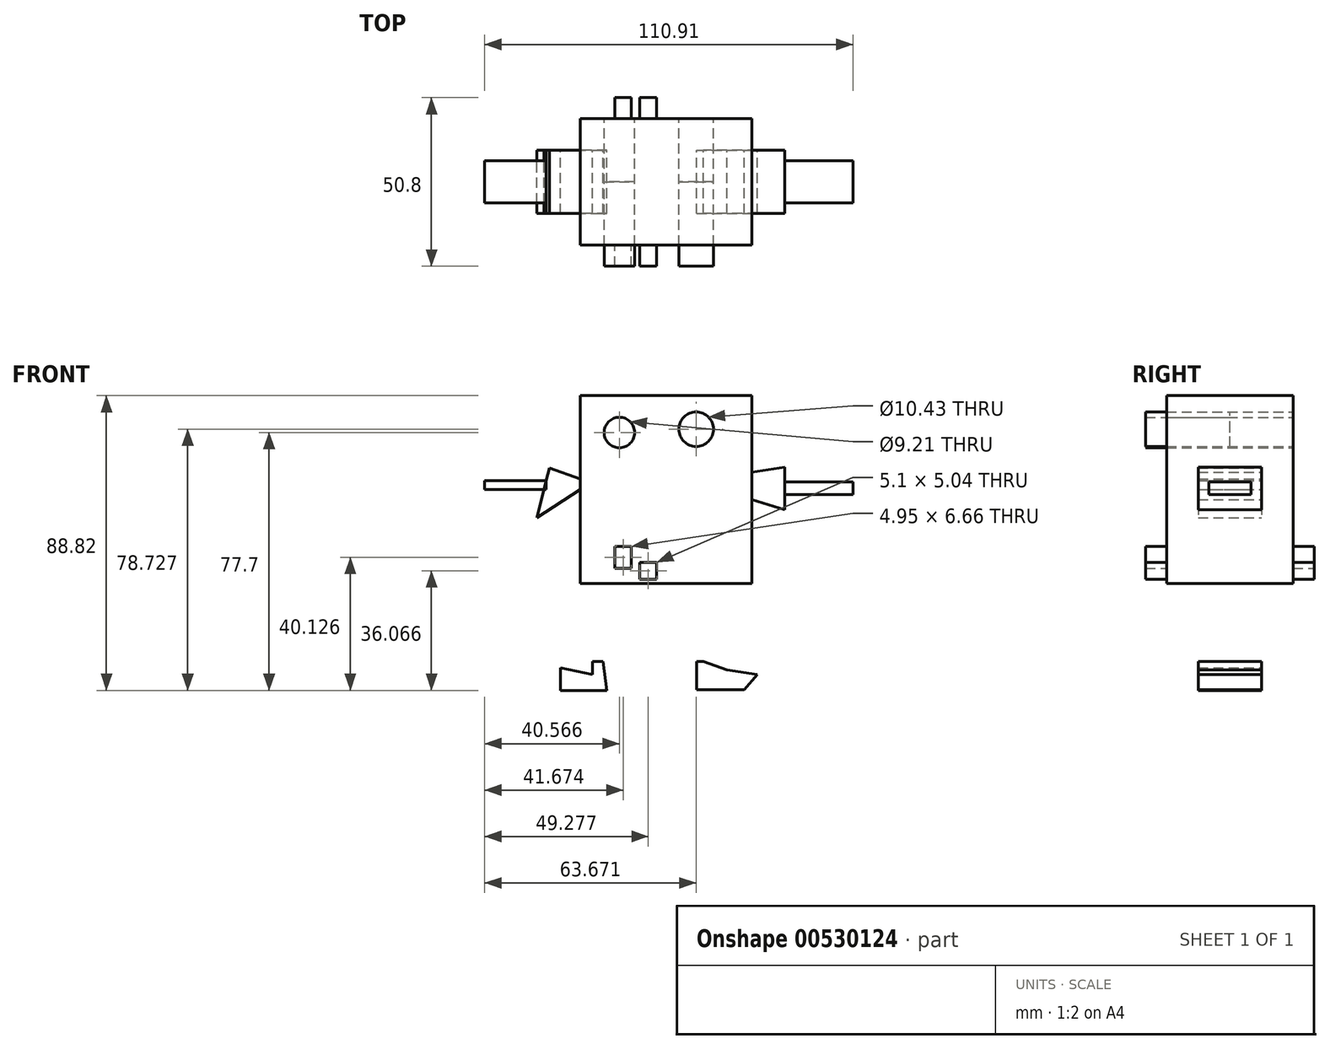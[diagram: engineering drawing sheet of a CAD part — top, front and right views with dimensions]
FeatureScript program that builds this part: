
annotation { "Feature Type Name" : "Feature", "Feature Type Description" : "" }
export const myFeature = defineFeature(function(context is Context, id is Id, definition is map)
    precondition{}
    {
        {
            var Q0;
            Q0=qCreatedBy(makeId("Front.planeOp"),FACE);
            var sketch = newSketch(context, id + "F0", { "sketchPlane" : qUnion([Q0])});
            skLineSegment(sketch, "E0.bottom", {"start": v(-25.84, -28.32) * mm, "end": v(25.84, -28.32) * mm});
            skLineSegment(sketch, "E0.top", {"start": v(-25.84, 28.32) * mm, "end": v(25.84, 28.32) * mm});
            skLineSegment(sketch, "E0.left", {"start": v(-25.84, -28.32) * mm, "end": v(-25.84, 28.32) * mm});
            skLineSegment(sketch, "E0.right", {"start": v(25.84, -28.32) * mm, "end": v(25.84, 28.32) * mm});
            skPoint(sketch, "E0.middle", {"position": v(0, 0) * mm});
            skCircle(sketch, "E1", {"center": v(-14.03, 17.2) * mm, "radius": 4.6 * mm});
            skCircle(sketch, "E2", {"center": v(9.07, 18.23) * mm, "radius": 5.22 * mm});
            skFitSpline(sketch, "E3", {"points": [v(-5.82, 8.64) * mm, v(-4.62, -11.72) * mm, v(3.08, 6.42) * mm], "startDerivative": vector(-0.94, -59.8) * mm, "endDerivative": vector(18.8, 55.68) * mm});
            skArc(sketch, "E4", {"start": v(-14.55, -10.7) * mm, "mid": v(0.62, -22.74) * mm, "end": v(18.65, -15.66) * mm});
            skLineSegment(sketch, "E5.bottom", {"start": v(-10.45, -17.04) * mm, "end": v(-15.4, -17.04) * mm});
            skLineSegment(sketch, "E5.top", {"start": v(-10.45, -23.7) * mm, "end": v(-15.4, -23.7) * mm});
            skLineSegment(sketch, "E5.left", {"start": v(-10.45, -17.04) * mm, "end": v(-10.45, -23.7) * mm});
            skLineSegment(sketch, "E5.right", {"start": v(-15.4, -17.04) * mm, "end": v(-15.4, -23.7) * mm});
            skLineSegment(sketch, "E6.bottom", {"start": v(-2.77, -21.91) * mm, "end": v(-7.87, -21.91) * mm});
            skLineSegment(sketch, "E6.top", {"start": v(-2.77, -26.96) * mm, "end": v(-7.87, -26.96) * mm});
            skLineSegment(sketch, "E6.left", {"start": v(-2.77, -21.91) * mm, "end": v(-2.77, -26.96) * mm});
            skLineSegment(sketch, "E6.right", {"start": v(-7.87, -21.91) * mm, "end": v(-7.87, -26.96) * mm});
            skLineSegment(sketch, "E7.bottom", {"start": v(-22.08, -28.32) * mm, "end": v(-19, -28.32) * mm});
            skLineSegment(sketch, "E7.top", {"start": v(-22.08, -51.77) * mm, "end": v(-19, -51.77) * mm});
            skLineSegment(sketch, "E7.left", {"start": v(-22.08, -28.32) * mm, "end": v(-22.08, -51.77) * mm});
            skLineSegment(sketch, "E7.right", {"start": v(-19, -28.32) * mm, "end": v(-19, -51.77) * mm});
            skLineSegment(sketch, "E8.bottom", {"start": v(9.24, -28.32) * mm, "end": v(11.3, -28.32) * mm});
            skLineSegment(sketch, "E8.top", {"start": v(9.24, -51.77) * mm, "end": v(11.3, -51.77) * mm});
            skLineSegment(sketch, "E8.left", {"start": v(9.24, -28.32) * mm, "end": v(9.24, -51.77) * mm});
            skLineSegment(sketch, "E8.right", {"start": v(11.3, -28.32) * mm, "end": v(11.3, -51.77) * mm});
            skLineSegment(sketch, "E9", {"start": v(-19, -51.77) * mm, "end": v(-17.8, -60.5) * mm});
            skLineSegment(sketch, "E10", {"start": v(-17.8, -60.5) * mm, "end": v(-31.83, -60.5) * mm});
            skLineSegment(sketch, "E11", {"start": v(-31.83, -60.5) * mm, "end": v(-31.83, -53.65) * mm});
            skLineSegment(sketch, "E12", {"start": v(-31.83, -53.65) * mm, "end": v(-22.08, -55.7) * mm});
            skLineSegment(sketch, "E13", {"start": v(-22.08, -55.7) * mm, "end": v(-22.08, -51.77) * mm});
            skLineSegment(sketch, "E14", {"start": v(9.24, -51.77) * mm, "end": v(9.24, -60.33) * mm});
            skLineSegment(sketch, "E15", {"start": v(9.24, -60.33) * mm, "end": v(23.62, -60.33) * mm});
            skLineSegment(sketch, "E16", {"start": v(23.62, -60.33) * mm, "end": v(27.55, -55.7) * mm});
            skLineSegment(sketch, "E17", {"start": v(27.55, -55.7) * mm, "end": v(18.31, -54.34) * mm});
            skLineSegment(sketch, "E18", {"start": v(18.31, -54.34) * mm, "end": v(11.3, -51.77) * mm});
            skLineSegment(sketch, "E19", {"start": v(-25.84, 3.17) * mm, "end": v(-35.12, 6.56) * mm});
            skLineSegment(sketch, "E20", {"start": v(-35.12, 6.56) * mm, "end": v(-38.85, -8.47) * mm});
            skLineSegment(sketch, "E21", {"start": v(-38.85, -8.47) * mm, "end": v(-25.84, 0) * mm});
            skLineSegment(sketch, "E22", {"start": v(25.84, 5.22) * mm, "end": v(35.77, 6.76) * mm});
            skLineSegment(sketch, "E23", {"start": v(35.77, 6.76) * mm, "end": v(35.77, -6.08) * mm});
            skLineSegment(sketch, "E24", {"start": v(35.77, -6.08) * mm, "end": v(25.84, -3) * mm});
            skLineSegment(sketch, "E25.bottom", {"start": v(-36.07, 2.73) * mm, "end": v(-54.6, 2.73) * mm});
            skLineSegment(sketch, "E25.top", {"start": v(-36.07, 0) * mm, "end": v(-54.6, 0) * mm});
            skLineSegment(sketch, "E25.left", {"start": v(-36.07, 2.73) * mm, "end": v(-36.07, 0) * mm});
            skLineSegment(sketch, "E25.right", {"start": v(-54.6, 2.73) * mm, "end": v(-54.6, 0) * mm});
            skLineSegment(sketch, "E26.bottom", {"start": v(35.77, 2.31) * mm, "end": v(56.3, 2.31) * mm});
            skLineSegment(sketch, "E26.top", {"start": v(35.77, -1.45) * mm, "end": v(56.3, -1.45) * mm});
            skLineSegment(sketch, "E26.left", {"start": v(35.77, 2.31) * mm, "end": v(35.77, -1.45) * mm});
            skLineSegment(sketch, "E26.right", {"start": v(56.3, 2.31) * mm, "end": v(56.3, -1.45) * mm});
            skSolve(sketch);
        }
        {
            var Q0;
            Q0=makeQuery(id+"F0.imprint","IMPRINT",FACE,{"disambiguationData":[TD([[makeQuery(id+"F0.imprint","IMPRINT",EDGE,{"derivedFrom":sQuery(id+"F0.wireOp",EDGE,"E1")}),1.0]])]});
            var Q1;
            Q1=makeQuery(id+"F0.imprint","IMPRINT",FACE,{"disambiguationData":[TD([[makeQuery(id+"F0.imprint","IMPRINT",EDGE,{"derivedFrom":sQuery(id+"F0.wireOp",EDGE,"E2")}),1.0]])]});
            extrude(context, id + "F1", {"entities" : qUnion([Q0, Q1]), "depth" : 25.4 * mm, "offsetDistance" : 25.4 * mm});
        }
        {
            var Q0;
            {var subQ1=sQuery(id+"F0.wireOp",EDGE,"E0.top");Q0=makeQuery(id+"F0.imprint","IMPRINT",FACE,{"disambiguationData":[TD([[makeQuery(id+"F0.imprint","IMPRINT",EDGE,{"derivedFrom":subQ1}),-1.0]])]});}
            extrude(context, id + "F2", {"entities" : qUnion([Q0]), "endBound" : BoundingType.SYMMETRIC, "depth" : 38.1 * mm, "offsetDistance" : 25.4 * mm});
        }
        {
            var Q0;
            Q0=makeQuery(id+"F0.imprint","IMPRINT",FACE,{"disambiguationData":[TD([[makeQuery(id+"F0.imprint","IMPRINT",EDGE,{"derivedFrom":sQuery(id+"F0.wireOp",EDGE,"E26.bottom")}),-1.0]])]});
            var Q1;
            Q1=makeQuery(id+"F0.imprint","IMPRINT",FACE,{"disambiguationData":[TD([[makeQuery(id+"F0.imprint","IMPRINT",EDGE,{"derivedFrom":sQuery(id+"F0.wireOp",EDGE,"E8.bottom")}),-1.0]])]});
            var Q2;
            Q2=makeQuery(id+"F0.imprint","IMPRINT",FACE,{"disambiguationData":[TD([[makeQuery(id+"F0.imprint","IMPRINT",EDGE,{"derivedFrom":sQuery(id+"F0.wireOp",EDGE,"E7.bottom")}),-1.0]])]});
            var Q3;
            {var subQ0=sQuery(id+"F0.wireOp",EDGE,"E25.bottom");Q3=makeQuery(id+"F0.imprint","IMPRINT",FACE,{"disambiguationData":[TD([[makeQuery(id+"F0.imprint","IMPRINT",EDGE,{"derivedFrom":subQ0}),1.0]])]});}
            extrude(context, id + "F3", {"entities" : qUnion([Q0, Q1, Q2, Q3]), "operationType" : NewBodyOperationType.ADD, "endBound" : BoundingType.SYMMETRIC, "depth" : 12.7 * mm, "offsetDistance" : 25.4 * mm});
        }
        {
            var Q0;
            {var subQ3=sQuery(id+"F0.wireOp",EDGE,"E22");Q0=makeQuery(id+"F0.imprint","IMPRINT",FACE,{"disambiguationData":[TD([[makeQuery(id+"F0.imprint","IMPRINT",EDGE,{"derivedFrom":subQ3}),-1.0]])]});}
            var Q1;
            Q1=makeQuery(id+"F0.imprint","IMPRINT",FACE,{"disambiguationData":[TD([[makeQuery(id+"F0.imprint","IMPRINT",EDGE,{"derivedFrom":sQuery(id+"F0.wireOp",EDGE,"E8.top")}),-1.0]])]});
            var Q2;
            Q2=makeQuery(id+"F0.imprint","IMPRINT",FACE,{"disambiguationData":[TD([[makeQuery(id+"F0.imprint","IMPRINT",EDGE,{"derivedFrom":sQuery(id+"F0.wireOp",EDGE,"E7.top")}),-1.0]])]});
            var Q3;
            {var subQ4=sQuery(id+"F0.wireOp",EDGE,"E19");Q3=makeQuery(id+"F0.imprint","IMPRINT",FACE,{"disambiguationData":[TD([[makeQuery(id+"F0.imprint","IMPRINT",EDGE,{"derivedFrom":subQ4}),1.0]])]});}
            extrude(context, id + "F4", {"entities" : qUnion([Q0, Q1, Q2, Q3]), "endBound" : BoundingType.SYMMETRIC, "depth" : 19.05 * mm, "offsetDistance" : 25.4 * mm});
        }
        {
            var Q0;
            Q0=sQuery(id+"F0.wireOp",EDGE,"E3");
            extrude(context, id + "F5", {"bodyType" : ToolBodyType.SURFACE, "surfaceEntities" : qUnion([Q0]), "endBound" : BoundingType.SYMMETRIC, "depth" : 76.2 * mm, "offsetDistance" : 25.4 * mm});
        }
        {
            var Q0;
            Q0=makeQuery(id+"F0.imprint","IMPRINT",FACE,{"disambiguationData":[TD([[makeQuery(id+"F0.imprint","IMPRINT",EDGE,{"derivedFrom":sQuery(id+"F0.wireOp",EDGE,"E5.bottom")}),1.0]])]});
            var Q1;
            Q1=makeQuery(id+"F0.imprint","IMPRINT",FACE,{"disambiguationData":[TD([[makeQuery(id+"F0.imprint","IMPRINT",EDGE,{"derivedFrom":sQuery(id+"F0.wireOp",EDGE,"E6.bottom")}),1.0]])]});
            extrude(context, id + "F6", {"entities" : qUnion([Q0, Q1]), "operationType" : NewBodyOperationType.ADD, "endBound" : BoundingType.SYMMETRIC, "depth" : 50.8 * mm, "offsetDistance" : 25.4 * mm});
        }
        {
            var Q0;
            Q0=sQuery(id+"F0.wireOp",EDGE,"E4");
            extrude(context, id + "F7", {"bodyType" : ToolBodyType.SURFACE, "surfaceEntities" : qUnion([Q0]), "endBound" : BoundingType.SYMMETRIC, "depth" : 50.8 * mm, "offsetDistance" : 25.4 * mm});
        }
    });
